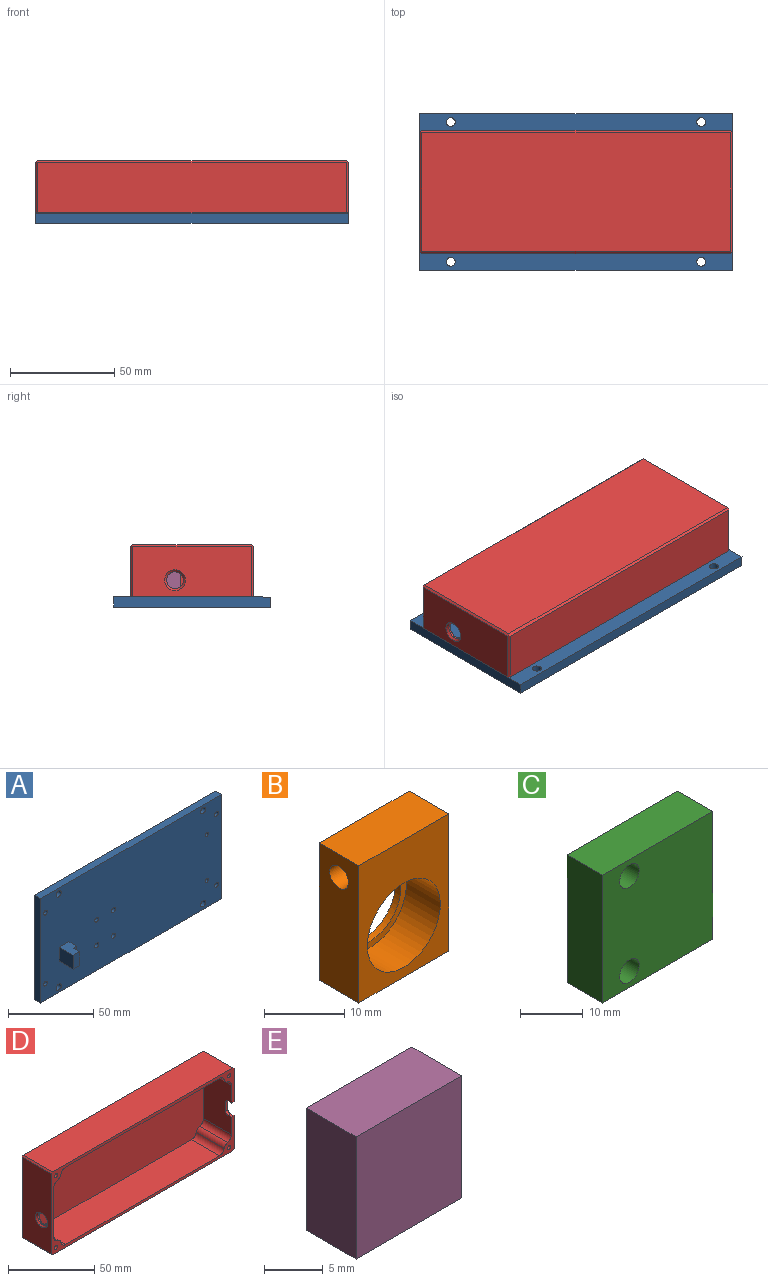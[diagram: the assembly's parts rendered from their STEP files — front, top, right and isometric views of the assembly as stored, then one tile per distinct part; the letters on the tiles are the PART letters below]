
ASSEMBLY  parts=5 mates=4
PART A: 35 faces, bbox 150x16.5x75 mm
  f0: plane 10x3mm, normal (0,-1,0), area 30mm2, adj f29,f31,f32,f33
  f1: plane 150x75mm, normal (0,-1,0), area 11038.4mm2, adj f2,f3,f4,f5,f6,f7,f8,f9
  f2: cylinder r=1.6mm len=3.2mm, axis (0,-1,0), area 20.1mm2, adj f1,f27
  f3: cylinder r=1.6mm len=3.2mm, axis (0,-1,0), area 20.1mm2, adj f1,f25
  f4: cylinder r=1.6mm len=3.2mm, axis (0,-1,0), area 20.1mm2, adj f1,f23
  f5: cylinder r=1.6mm len=3.2mm, axis (0,-1,0), area 20.1mm2, adj f1,f21
  f6: plane 75x5mm, normal (-1,0,0), area 375mm2, adj f1,f7,f9,f10
  f7: plane 150x5mm, normal (0,0,-1), area 750mm2, adj f1,f6,f8,f10
  f8: plane 75x5mm, normal (1,0,0), area 375mm2, adj f1,f7,f9,f10
  f9: plane 150x5mm, normal (0,0,1), area 750mm2, adj f1,f6,f8,f10
  f10: plane 150x75mm, normal (0,1,0), area 11037.5mm2, adj f6,f7,f8,f9,f11,f12,f13,f14
  f11: cylinder r=1.25mm len=5mm, axis (0,-1,0), area 39.3mm2, adj f1,f10
  f12: cylinder r=1.25mm len=5mm, axis (0,-1,0), area 39.3mm2, adj f1,f10
  f13: cylinder r=1.65mm len=5mm, axis (0,-1,0), area 51.8mm2, adj f1,f10
  f14: cylinder r=1.65mm len=5mm, axis (0,-1,0), area 51.8mm2, adj f1,f10
  f15: cylinder r=1.65mm len=5mm, axis (0,-1,0), area 51.8mm2, adj f1,f10
  f16: cylinder r=1.65mm len=5mm, axis (0,-1,0), area 51.8mm2, adj f1,f10
  f17: cylinder r=2.1mm len=5mm, axis (0,-1,0), area 66mm2, adj f1,f10
  f18: cylinder r=2.1mm len=5mm, axis (0,-1,0), area 66mm2, adj f1,f10
  f19: cylinder r=2.1mm len=5mm, axis (0,-1,0), area 66mm2, adj f1,f10
  f20: cylinder r=2.1mm len=5mm, axis (0,-1,0), area 66mm2, adj f1,f10
  f21: plane 6x6mm, normal (0,1,0), area 20.2mm2, adj f5,f22
  f22: cylinder r=3mm len=6mm, axis (0,1,0), area 56.5mm2, adj f10,f21
  f23: plane 6x6mm, normal (0,1,0), area 20.2mm2, adj f4,f24
  f24: cylinder r=3mm len=6mm, axis (0,1,0), area 56.5mm2, adj f10,f23
  f25: plane 6x6mm, normal (0,1,0), area 20.2mm2, adj f3,f26
  f26: cylinder r=3mm len=6mm, axis (0,1,0), area 56.5mm2, adj f10,f25
  f27: plane 6x6mm, normal (0,1,0), area 20.2mm2, adj f2,f28
  f28: cylinder r=3mm len=6mm, axis (0,1,0), area 56.5mm2, adj f10,f27
  f29: plane 11.45x8mm, normal (0,0,1), area 76.6mm2, adj f0,f1,f30,f32,f33,f34
  f30: plane 11.45x10mm, normal (-1,0,0), area 114.5mm2, adj f1,f29,f31,f34
  f31: plane 11.45x8mm, normal (0,0,-1), area 76.6mm2, adj f0,f1,f30,f32,f33,f34
  f32: plane 10x6.45mm, normal (1,0,0), area 64.5mm2, adj f0,f1,f29,f31
  f33: plane 10x5mm, normal (1,0,0), area 50mm2, adj f0,f29,f31,f34
  f34: plane 10x5mm, normal (0,-1,0), area 50mm2, adj f29,f30,f31,f33
PART B: 11 faces, bbox 15.9x7x21 mm
  f0: plane 21x7mm, normal (-1,0,0), area 138.4mm2, adj f1,f3,f4,f5,f9
  f1: plane 15.9x7mm, normal (0,0,-1), area 111.3mm2, adj f0,f2,f4,f5
  f2: plane 21x7mm, normal (1,0,0), area 147mm2, adj f1,f3,f4,f5
  f3: plane 15.9x7mm, normal (0,0,1), area 111.3mm2, adj f0,f2,f4,f5
  f4: plane 21x15.9mm, normal (0,-1,0), area 203.2mm2, adj f0,f1,f2,f3,f6
  f5: plane 21x15.9mm, normal (0,1,0), area 238.9mm2, adj f0,f1,f2,f3,f8
  f6: cylinder r=6.45mm len=12.9mm, axis (0,-1,0), area 243.2mm2, adj f4,f7
  f7: plane 12.9x12.9mm, normal (0,-1,0), area 35.7mm2, adj f6,f8
  f8: cylinder r=5.5mm len=11mm, axis (0,-1,0), area 34.6mm2, adj f5,f7
  f9: cylinder r=1.65mm len=10mm, axis (-1,0,0), area 103.7mm2, adj f0,f10
  f10: plane 3.3x3.3mm, normal (-1,0,0), area 8.6mm2, adj f9
PART C: 8 faces, bbox 24.9x8x24.9 mm
  f0: plane 24.9x7.95mm, normal (-1,0,0), area 198mm2, adj f1,f3,f4,f5
  f1: plane 24.9x7.95mm, normal (0,0,-1), area 198mm2, adj f0,f2,f4,f5
  f2: plane 24.9x7.95mm, normal (1,0,0), area 198mm2, adj f1,f3,f4,f5
  f3: plane 24.9x7.95mm, normal (0,0,1), area 198mm2, adj f0,f2,f4,f5
  f4: plane 24.9x24.9mm, normal (0,-1,0), area 589.6mm2, adj f0,f1,f2,f3,f6,f7
  f5: plane 24.9x24.9mm, normal (0,1,0), area 589.6mm2, adj f0,f1,f2,f3,f6,f7
  f6: cylinder r=2.2mm len=7.95mm, axis (0,-1,0), area 109.9mm2, adj f4,f5
  f7: cylinder r=2.2mm len=7.95mm, axis (0,-1,0), area 109.9mm2, adj f4,f5
PART D: 46 faces, bbox 150x25x59 mm
  f0: plane 35.19x23mm, normal (-1,0,0), area 761.2mm2, adj f1,f2,f24,f28,f32,f33,f34,f35
  f1: plane 150x59mm, normal (0,-1,0), area 938.9mm2, adj f0,f3,f4,f5,f6,f7,f8,f9
  f2: plane 146x55mm, normal (0,-1,0), area 7869.5mm2, adj f0,f3,f4,f5,f19,f20,f21,f22
  f3: plane 126x23mm, normal (0,0,1), area 2898mm2, adj f1,f2,f26,f29
  f4: plane 126.19x23mm, normal (0,0,-1), area 2902.4mm2, adj f1,f2,f21,f22
  f5: plane 35x23mm, normal (1,0,0), area 754.7mm2, adj f1,f2,f19,f25,f31
  f6: plane 57x24mm, normal (-1,0,0), area 1289.5mm2, adj f1,f37,f38,f44,f45
  f7: plane 148x24mm, normal (0,0,-1), area 3552mm2, adj f1,f39,f42,f45
  f8: plane 57x24mm, normal (1,0,0), area 1319.7mm2, adj f1,f32,f33,f34,f35,f36,f41,f42
  f9: plane 148x24mm, normal (0,0,1), area 3552mm2, adj f1,f40,f43,f44
  f10: plane 148x57mm, normal (0,1,0), area 8436mm2, adj f38,f39,f40,f41
  f11: cylinder r=1.25mm len=10mm, axis (0,-1,0), area 78.5mm2, adj f1,f12
  f12: plane 2.5x2.5mm, normal (0,-1,0), area 4.9mm2, adj f11
  f13: cylinder r=1.25mm len=10mm, axis (0,-1,0), area 78.5mm2, adj f1,f14
  f14: plane 2.5x2.5mm, normal (0,-1,0), area 4.9mm2, adj f13
  f15: cylinder r=1.25mm len=10mm, axis (0,-1,0), area 78.5mm2, adj f1,f16
  f16: plane 2.5x2.5mm, normal (0,-1,0), area 4.9mm2, adj f15
  f17: cylinder r=1.25mm len=10mm, axis (0,-1,0), area 78.5mm2, adj f1,f18
  f18: plane 2.5x2.5mm, normal (0,-1,0), area 4.9mm2, adj f17
  f19: cylinder r=4mm len=23mm, axis (0,-1,0), area 121.3mm2, adj f1,f2,f5,f20
  f20: cylinder r=4mm len=23mm, axis (0,-1,0), area 101mm2, adj f1,f2,f19,f21
  f21: cylinder r=4mm len=23mm, axis (0,-1,0), area 124.3mm2, adj f1,f2,f4,f20
  f22: cylinder r=4mm len=23mm, axis (0,1,0), area 121.3mm2, adj f1,f2,f4,f23
  f23: cylinder r=4mm len=23mm, axis (0,1,0), area 101mm2, adj f1,f2,f22,f24
  f24: cylinder r=4mm len=23mm, axis (0,1,0), area 124.3mm2, adj f0,f1,f2,f23
  f25: cylinder r=4mm len=23mm, axis (0,1,0), area 123.7mm2, adj f1,f2,f5,f27
  f26: cylinder r=4mm len=23mm, axis (0,-1,0), area 123.7mm2, adj f1,f2,f3,f27
  f27: cylinder r=4mm len=23mm, axis (0,1,0), area 102.9mm2, adj f1,f2,f25,f26
  f28: cylinder r=4mm len=23mm, axis (0,1,0), area 123.7mm2, adj f0,f1,f2,f30
  f29: cylinder r=4mm len=23mm, axis (0,1,0), area 123.7mm2, adj f1,f2,f3,f30
  f30: cylinder r=4mm len=23mm, axis (0,1,0), area 102.9mm2, adj f1,f2,f28,f29
  f31: cylinder r=4mm len=8mm, axis (-1,0,0), area 25.1mm2, adj f5,f37
  f32: plane 3x2mm, normal (0,0,-1), area 6mm2, adj f0,f1,f8,f35
  f33: plane 3x2mm, normal (0,0,1), area 6mm2, adj f0,f1,f8,f36
  f34: plane 6x2mm, normal (0,-1,0), area 12mm2, adj f0,f8,f35,f36
  f35: cylinder r=2mm len=2mm, axis (-1,0,0), area 6.3mm2, adj f0,f8,f32,f34
  f36: cylinder r=2mm len=2mm, axis (1,0,0), area 6.3mm2, adj f0,f8,f33,f34
  f37: cone r=4mm half-angle=45deg, axis (-1,0,0), area 40mm2, adj f6,f31
  f38: plane 58x1mm, normal (-0.71,0.71,0), area 81.3mm2, adj f6,f10,f39,f40,f44,f45
  f39: plane 149x1mm, normal (0,0.71,-0.71), area 210mm2, adj f7,f10,f38,f41,f42,f45
  f40: plane 149x1mm, normal (0,0.71,0.71), area 210mm2, adj f9,f10,f38,f41,f43,f44
  f41: plane 58x1mm, normal (0.71,0.71,0), area 81.3mm2, adj f8,f10,f39,f40,f42,f43
  f42: plane 24.5x1mm, normal (0.71,0,-0.71), area 34.3mm2, adj f1,f7,f8,f39,f41
  f43: plane 24.5x1mm, normal (0.71,0,0.71), area 34.3mm2, adj f1,f8,f9,f40,f41
  f44: plane 24.5x1mm, normal (-0.71,0,0.71), area 34.3mm2, adj f1,f6,f9,f38,f40
  f45: plane 24.5x1mm, normal (-0.71,0,-0.71), area 34.3mm2, adj f1,f6,f7,f38,f39
PART E: 6 faces, bbox 12.7x6x12.7 mm
  f0: plane 12.7x6mm, normal (-1,0,0), area 76.2mm2, adj f1,f3,f4,f5
  f1: plane 12.7x6mm, normal (0,0,-1), area 76.2mm2, adj f0,f2,f4,f5
  f2: plane 12.7x6mm, normal (1,0,0), area 76.2mm2, adj f1,f3,f4,f5
  f3: plane 12.7x6mm, normal (0,0,1), area 76.2mm2, adj f0,f2,f4,f5
  f4: plane 12.7x12.7mm, normal (0,-1,0), area 161.3mm2, adj f0,f1,f2,f3
  f5: plane 12.7x12.7mm, normal (0,1,0), area 161.3mm2, adj f0,f1,f2,f3
PLACE A rot(axis=(-1,0,0),89.9deg) t=(0,-1.41,98.65)mm fixed
PLACE B rot(axis=(0,0,1),90deg) t=(29.91,18.23,103.7)mm
PLACE C rot(axis=(-1,0,0),89.9deg) t=(40.4,13.58,103.69)mm
PLACE D rot(axis=(1,0,0),90.1deg) t=(0,65.52,128.8)mm
PLACE E rot(axis=(0,0,-1),45deg) t=(21.65,54.71,103.77)mm
MATE fastened D.f13 <-> A.f2  axis (0,0,-1) through (146,10.58,103.68)mm
MATE fastened A.f15 <-> C.f6  axis (0,0,1) through (46.5,16.78,103.69)mm
MATE parallel B.f1 <-> A.f1  axis (0,0,-1) through (33.41,26.18,103.71)mm
MATE parallel E.f1 <-> A.f1  axis (0,0,-1) through (24.02,48.1,103.76)mm
